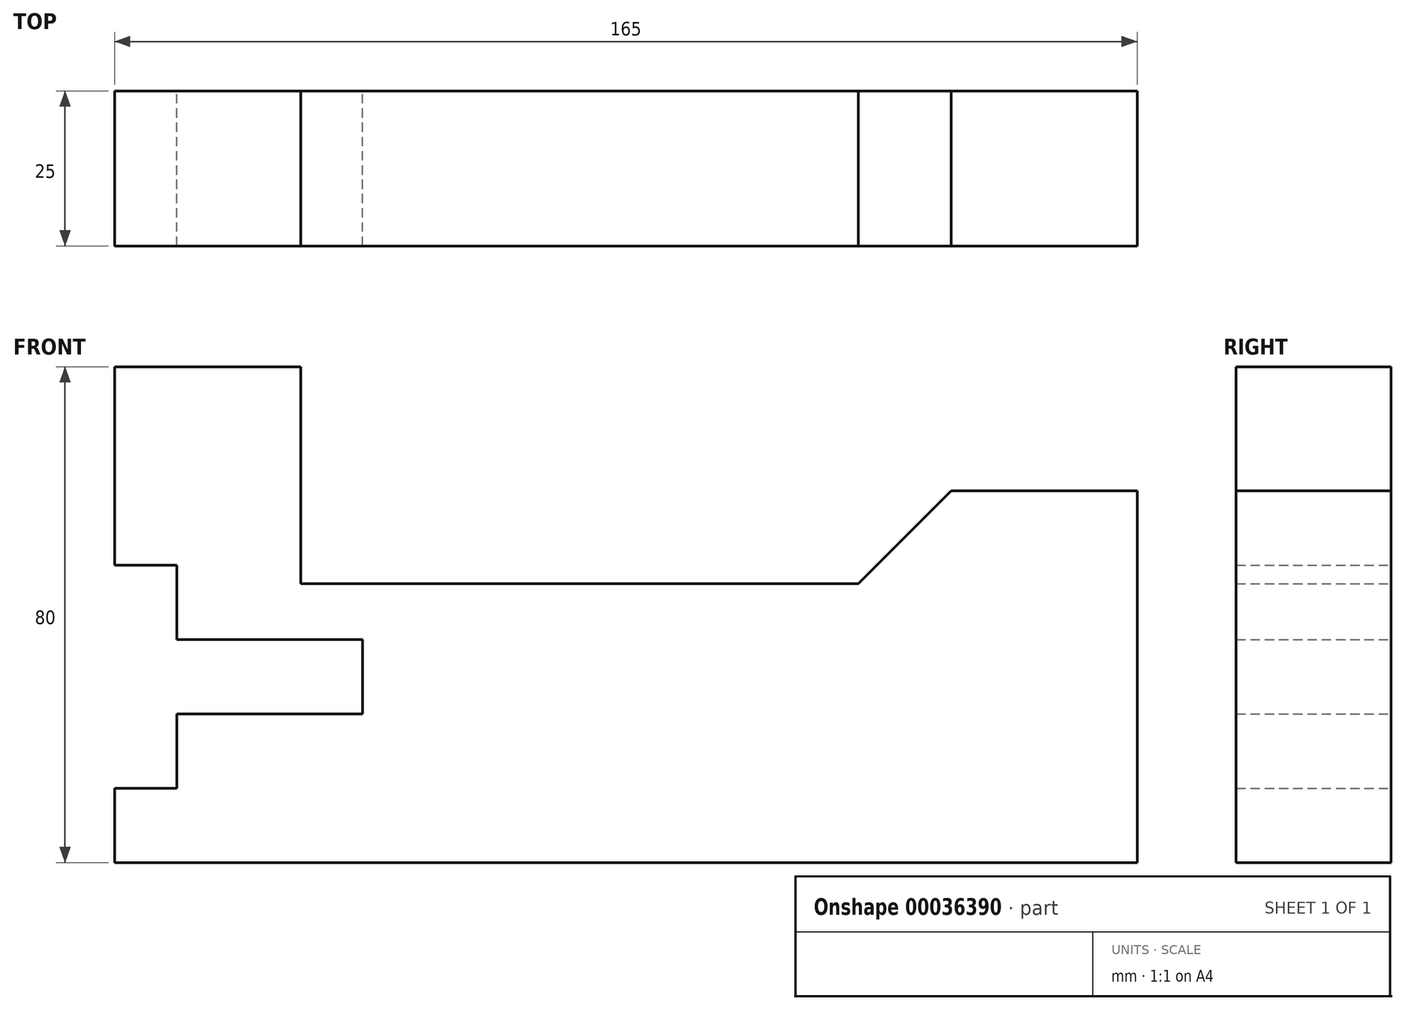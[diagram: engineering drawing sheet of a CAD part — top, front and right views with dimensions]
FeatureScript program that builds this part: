
annotation { "Feature Type Name" : "Feature", "Feature Type Description" : "" }
export const myFeature = defineFeature(function(context is Context, id is Id, definition is map)
    precondition{}
    {
        {
            var Q0;
            Q0=qCreatedBy(makeId("Front.planeOp"),FACE);
            var sketch = newSketch(context, id + "F0", { "sketchPlane" : qUnion([Q0])});
            skLineSegment(sketch, "E0", {"start": v(-82.5, 0) * mm, "end": v(82.5, 0) * mm});
            skLineSegment(sketch, "E1", {"start": v(82.5, 0) * mm, "end": v(82.5, 60) * mm});
            skLineSegment(sketch, "E2", {"start": v(82.5, 60) * mm, "end": v(52.5, 60) * mm});
            skLineSegment(sketch, "E3", {"start": v(52.5, 60) * mm, "end": v(37.5, 45) * mm});
            skLineSegment(sketch, "E4", {"start": v(37.5, 45) * mm, "end": v(-52.5, 45) * mm});
            skLineSegment(sketch, "E5", {"start": v(-52.5, 45) * mm, "end": v(-52.5, 80) * mm});
            skLineSegment(sketch, "E6", {"start": v(-52.5, 80) * mm, "end": v(-82.5, 80) * mm});
            skLineSegment(sketch, "E7", {"start": v(-82.5, 80) * mm, "end": v(-82.5, 48) * mm});
            skLineSegment(sketch, "E8", {"start": v(-82.5, 48) * mm, "end": v(-72.5, 48) * mm});
            skLineSegment(sketch, "E9", {"start": v(-72.5, 48) * mm, "end": v(-72.5, 36) * mm});
            skLineSegment(sketch, "E10", {"start": v(-72.5, 36) * mm, "end": v(-42.5, 36) * mm});
            skLineSegment(sketch, "E11", {"start": v(-42.5, 36) * mm, "end": v(-42.5, 24) * mm});
            skLineSegment(sketch, "E12", {"start": v(-42.5, 24) * mm, "end": v(-72.5, 24) * mm});
            skLineSegment(sketch, "E13", {"start": v(-72.5, 24) * mm, "end": v(-72.5, 12) * mm});
            skLineSegment(sketch, "E14", {"start": v(-72.5, 12) * mm, "end": v(-82.5, 12) * mm});
            skLineSegment(sketch, "E15", {"start": v(-82.5, 12) * mm, "end": v(-82.5, 0) * mm});
            skSolve(sketch);
        }
        {
            var Q0;
            Q0=makeQuery(id+"F0.imprint","IMPRINT",FACE,{"disambiguationData":[TD([[makeQuery(id+"F0.imprint","IMPRINT",EDGE,{"derivedFrom":sQuery(id+"F0.wireOp",EDGE,"E0")}),1.0]])]});
            extrude(context, id + "F1", {"entities" : qUnion([Q0]), "depth" : 25 * mm});
        }
    });
